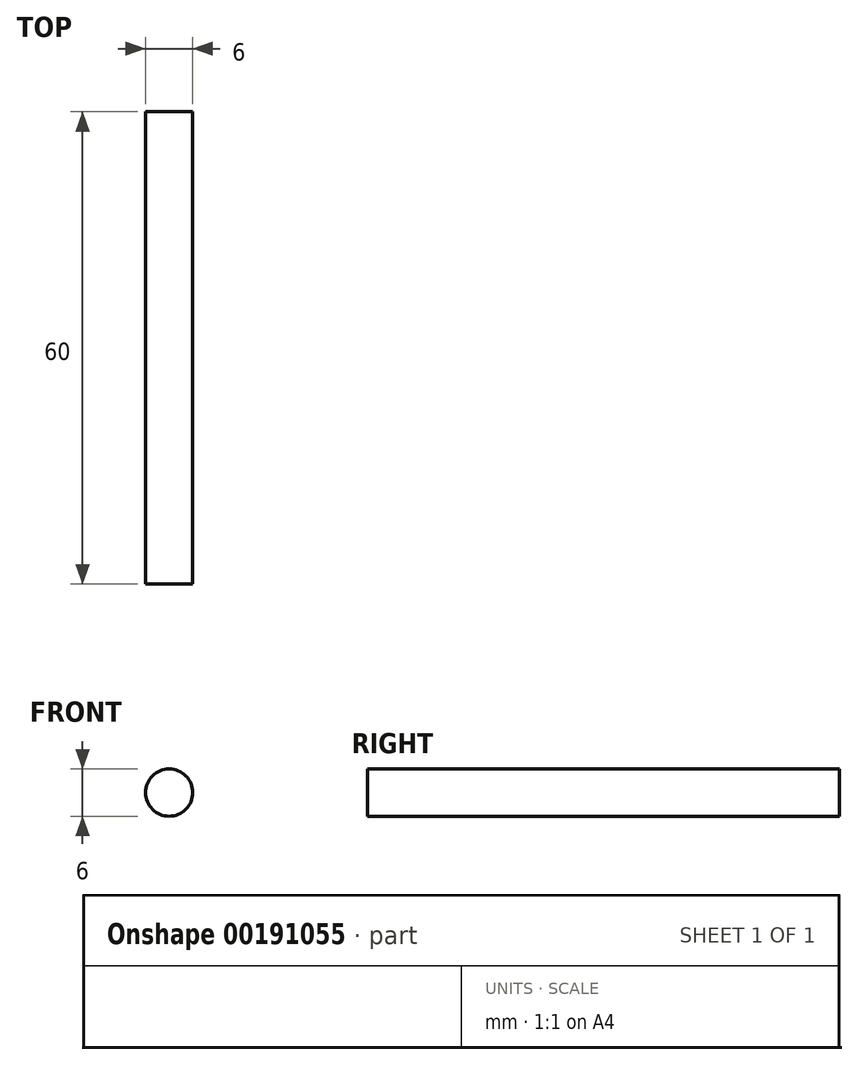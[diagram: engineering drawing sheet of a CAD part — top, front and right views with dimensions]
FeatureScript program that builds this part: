
annotation { "Feature Type Name" : "Feature", "Feature Type Description" : "" }
export const myFeature = defineFeature(function(context is Context, id is Id, definition is map)
    precondition{}
    {
        {
            var Q0;
            Q0=qCreatedBy(makeId("Front.planeOp"),FACE);
            var sketch = newSketch(context, id + "F0", { "sketchPlane" : qUnion([Q0])});
            skCircle(sketch, "E0", {"center": v(0, 0) * mm, "radius": 3 * mm});
            skSolve(sketch);
        }
        {
            var Q0;
            Q0 = qSketchRegion(id + "F0", true);
            extrude(context, id + "F1", {"entities" : qUnion([Q0]), "depth" : 60 * mm});
        }
    });
